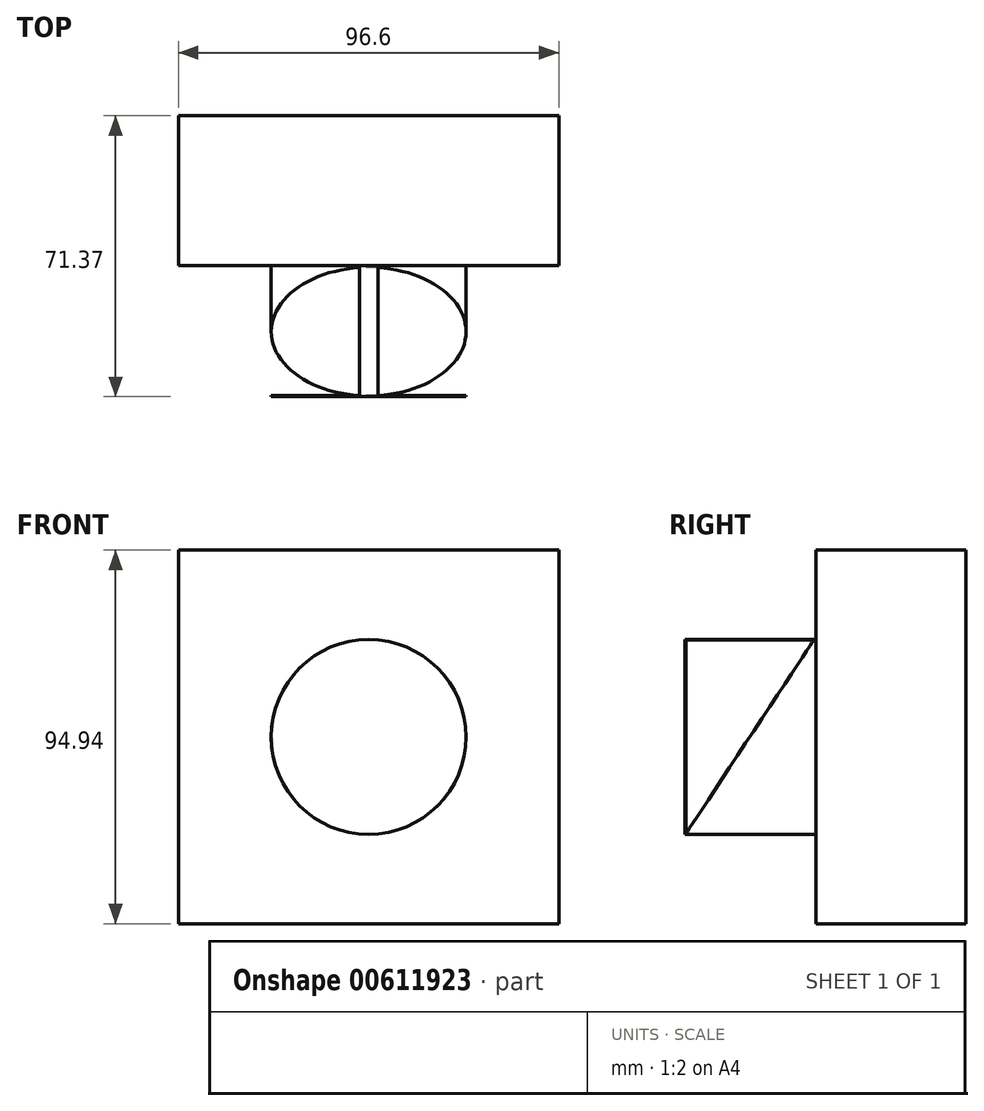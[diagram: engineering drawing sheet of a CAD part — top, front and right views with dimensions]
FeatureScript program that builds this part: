
annotation { "Feature Type Name" : "Feature", "Feature Type Description" : "" }
export const myFeature = defineFeature(function(context is Context, id is Id, definition is map)
    precondition{}
    {
        {
            var Q0;
            Q0=qCreatedBy(makeId("Front.planeOp"),FACE);
            var sketch = newSketch(context, id + "F0", { "sketchPlane" : qUnion([Q0])});
            skLineSegment(sketch, "E0.bottom", {"start": v(48.3, 47.47) * mm, "end": v(-48.3, 47.47) * mm});
            skLineSegment(sketch, "E0.top", {"start": v(48.3, -47.47) * mm, "end": v(-48.3, -47.47) * mm});
            skLineSegment(sketch, "E0.left", {"start": v(48.3, 47.47) * mm, "end": v(48.3, -47.47) * mm});
            skLineSegment(sketch, "E0.right", {"start": v(-48.3, 47.47) * mm, "end": v(-48.3, -47.47) * mm});
            skPoint(sketch, "E0.middle", {"position": v(0, 0) * mm});
            skSolve(sketch);
        }
        {
            var Q0;
            Q0 = qSketchRegion(id + "F0", true);
            extrude(context, id + "F1", {"entities" : qUnion([Q0]), "depth" : 38.1 * mm, "offsetDistance" : 25.4 * mm});
        }
        {
            var Q0;
            Q0=makeQuery(id+"F1.opExtrude","CAP_FACE",FACE,{"disambiguationData":[OSD([sQuery(id+"F0.wireOp",EDGE,"E0.bottom"),sQuery(id+"F0.wireOp",EDGE,"E0.top"),sQuery(id+"F0.wireOp",EDGE,"E0.left"),sQuery(id+"F0.wireOp",EDGE,"E0.right")])],"isStart":false});
            var sketch = newSketch(context, id + "F2", { "sketchPlane" : qUnion([Q0])});
            skCircle(sketch, "E1", {"center": v(0, 0) * mm, "radius": 24.76 * mm});
            skSolve(sketch);
        }
        {
            var Q0;
            Q0 = qSketchRegion(id + "F2", true);
            extrude(context, id + "F3", {"entities" : qUnion([Q0]), "operationType" : NewBodyOperationType.ADD, "depth" : 33.27 * mm, "offsetDistance" : 25.4 * mm});
        }
        {
            var Q0;
            Q0=qCreatedBy(makeId("Right.planeOp"),FACE);
            var sketch = newSketch(context, id + "F4", { "sketchPlane" : qUnion([Q0])});
            skLineSegment(sketch, "E2", {"start": v(-71.1, -24.65) * mm, "end": v(-38.59, 24.65) * mm});
            skLineSegment(sketch, "E3", {"start": v(-38.59, 24.65) * mm, "end": v(-71.1, 24.65) * mm});
            skLineSegment(sketch, "E4", {"start": v(-71.1, 24.65) * mm, "end": v(-71.1, -24.65) * mm});
            skSolve(sketch);
        }
        {
            var Q0;
            Q0 = qSketchRegion(id + "F4", true);
            extrude(context, id + "F5", {"entities" : qUnion([Q0]), "operationType" : NewBodyOperationType.REMOVE, "endBound" : BoundingType.SYMMETRIC, "depth" : 1270 * mm, "offsetDistance" : 25.4 * mm});
        }
    });
